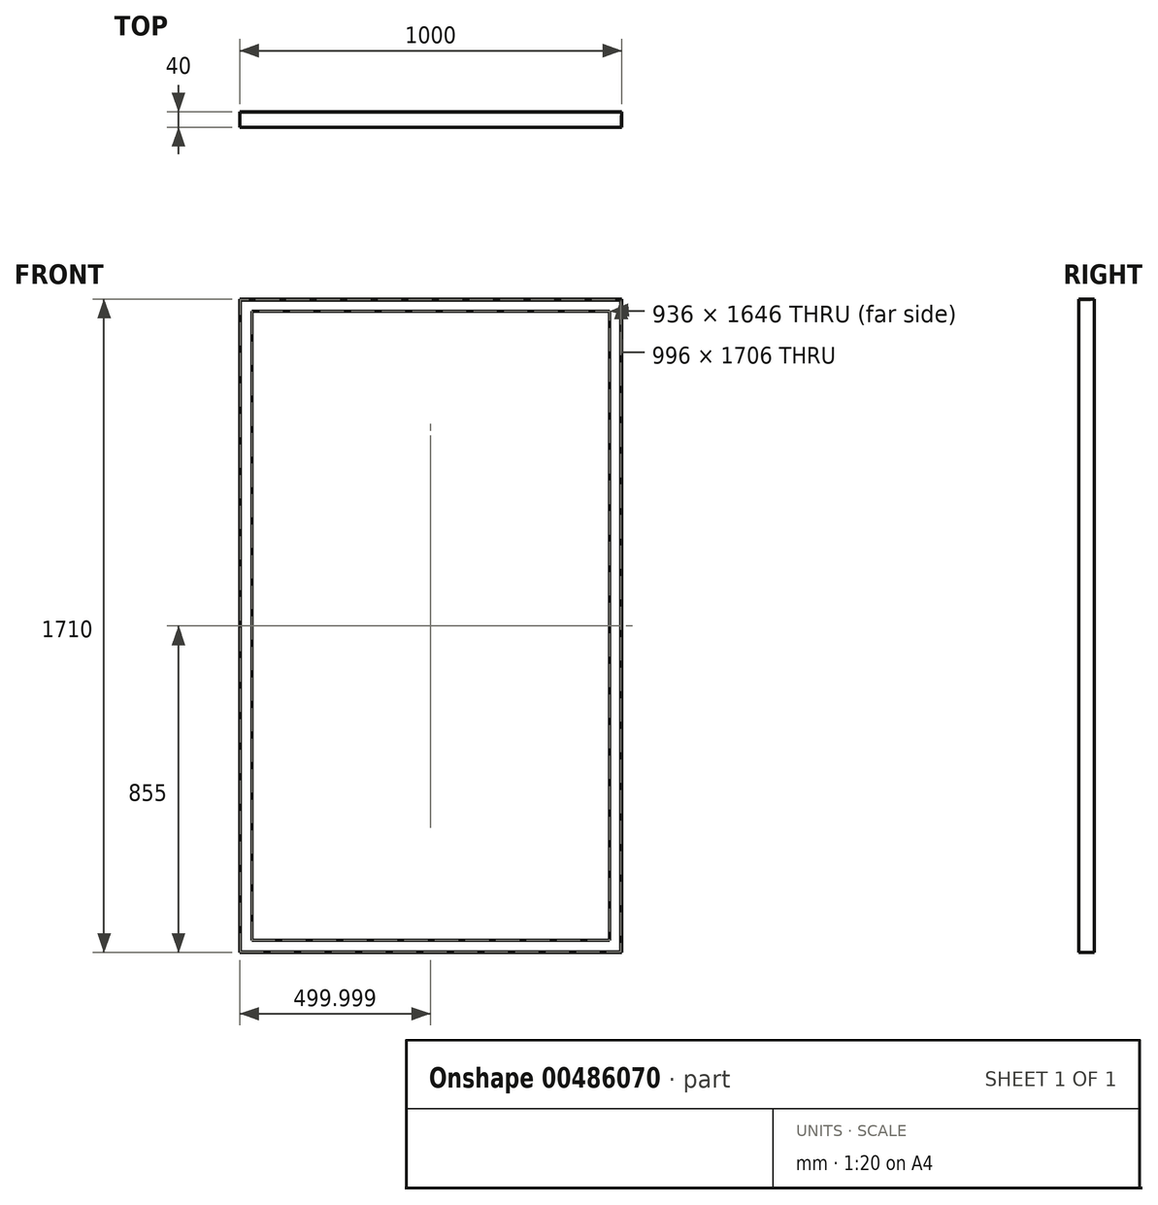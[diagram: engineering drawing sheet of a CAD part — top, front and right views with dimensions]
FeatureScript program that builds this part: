
annotation { "Feature Type Name" : "Feature", "Feature Type Description" : "" }
export const myFeature = defineFeature(function(context is Context, id is Id, definition is map)
    precondition{}
    {
        {
            var Q0;
            Q0=qCreatedBy(makeId("Front.planeOp"),FACE);
            var sketch = newSketch(context, id + "F0", { "sketchPlane" : qUnion([Q0])});
            skLineSegment(sketch, "E0.0", {"start": v(959.78, -40) * mm, "end": v(959.78, -1750) * mm});
            skLineSegment(sketch, "E1.0", {"start": v(-40.22, -40) * mm, "end": v(-40.22, -1750) * mm});
            skLineSegment(sketch, "E2.0", {"start": v(-40.22, -1750) * mm, "end": v(959.78, -1750) * mm});
            skLineSegment(sketch, "E3.0", {"start": v(-38.22, -42) * mm, "end": v(957.78, -42) * mm});
            skLineSegment(sketch, "E4.0", {"start": v(-38.22, -42) * mm, "end": v(-38.22, -1748) * mm});
            skLineSegment(sketch, "E5.0", {"start": v(-38.22, -1748) * mm, "end": v(957.78, -1748) * mm});
            skLineSegment(sketch, "E6.0", {"start": v(957.78, -42) * mm, "end": v(957.78, -1748) * mm});
            skLineSegment(sketch, "E7", {"start": v(959.78, -40) * mm, "end": v(-40.22, -40) * mm});
            skLineSegment(sketch, "E8.0", {"start": v(-38.22, -72) * mm, "end": v(957.78, -72) * mm});
            skLineSegment(sketch, "E9.0", {"start": v(-8.22, -42) * mm, "end": v(-8.22, -1749.66) * mm});
            skLineSegment(sketch, "E10.0", {"start": v(-38.22, -1718) * mm, "end": v(957.78, -1718) * mm});
            skLineSegment(sketch, "E11.0", {"start": v(927.78, -42) * mm, "end": v(927.78, -1749.66) * mm});
            skSolve(sketch);
        }
        {
            var Q0;
            Q0=qSketchRegion(id+"F0",true);
            extrude(context, id + "F1", {"entities" : qUnion([Q0]), "depth" : 40 * mm, "offsetDistance" : 25 * mm});
        }
        {
            var Q0;
            {var subQ0=sQuery(id+"F0.wireOp",EDGE,"E6.0");var subQ1=sQuery(id+"F0.wireOp",EDGE,"E3.0");var subQ2=makeQuery(id+"F0.imprint","INTERSECT",VERTEX,{"derivedFrom":[subQ1,subQ0]});Q0=makeQuery(id+"F0.imprint","IMPRINT",FACE,{"disambiguationData":[TD([[makeQuery(id+"F0.imprint","IMPRINT",EDGE,{"disambiguationData":[TD([[subQ2,1.0]])],"derivedFrom":subQ1}),-1.0]])]});}
            var Q1;
            {var subQ0=sQuery(id+"F0.wireOp",EDGE,"E9.0");var subQ1=sQuery(id+"F0.wireOp",EDGE,"E3.0");var subQ2=makeQuery(id+"F0.imprint","INTERSECT",VERTEX,{"derivedFrom":[subQ1,subQ0]});Q1=makeQuery(id+"F0.imprint","IMPRINT",FACE,{"disambiguationData":[TD([[makeQuery(id+"F0.imprint","IMPRINT",EDGE,{"disambiguationData":[TD([[subQ2,-1.0]])],"derivedFrom":subQ1}),-1.0]])]});}
            var Q2;
            {var subQ0=sQuery(id+"F0.wireOp",EDGE,"E8.0");var subQ1=sQuery(id+"F0.wireOp",EDGE,"E6.0");var subQ2=makeQuery(id+"F0.imprint","INTERSECT",VERTEX,{"derivedFrom":[subQ1,subQ0]});Q2=makeQuery(id+"F0.imprint","IMPRINT",FACE,{"disambiguationData":[TD([[makeQuery(id+"F0.imprint","IMPRINT",EDGE,{"disambiguationData":[TD([[subQ2,-1.0]])],"derivedFrom":subQ1}),-1.0]])]});}
            var Q3;
            {var subQ0=sQuery(id+"F0.wireOp",EDGE,"E4.0");var subQ1=sQuery(id+"F0.wireOp",EDGE,"E3.0");var subQ2=makeQuery(id+"F0.imprint","INTERSECT",VERTEX,{"derivedFrom":[subQ1,subQ0]});Q3=makeQuery(id+"F0.imprint","IMPRINT",FACE,{"disambiguationData":[TD([[makeQuery(id+"F0.imprint","IMPRINT",EDGE,{"disambiguationData":[TD([[subQ2,-1.0]])],"derivedFrom":subQ1}),-1.0]])]});}
            var Q4;
            {var subQ0=sQuery(id+"F0.wireOp",EDGE,"E8.0");var subQ1=sQuery(id+"F0.wireOp",EDGE,"E4.0");var subQ2=makeQuery(id+"F0.imprint","INTERSECT",VERTEX,{"derivedFrom":[subQ1,subQ0]});Q4=makeQuery(id+"F0.imprint","IMPRINT",FACE,{"disambiguationData":[TD([[makeQuery(id+"F0.imprint","IMPRINT",EDGE,{"disambiguationData":[TD([[subQ2,-1.0]])],"derivedFrom":subQ1}),1.0]])]});}
            var Q5;
            {var subQ0=sQuery(id+"F0.wireOp",EDGE,"E5.0");var subQ1=sQuery(id+"F0.wireOp",EDGE,"E4.0");var subQ2=makeQuery(id+"F0.imprint","INTERSECT",VERTEX,{"derivedFrom":[subQ1,subQ0]});Q5=makeQuery(id+"F0.imprint","IMPRINT",FACE,{"disambiguationData":[TD([[makeQuery(id+"F0.imprint","IMPRINT",EDGE,{"disambiguationData":[TD([[subQ2,1.0]])],"derivedFrom":subQ1}),1.0]])]});}
            var Q6;
            {var subQ0=sQuery(id+"F0.wireOp",EDGE,"E9.0");var subQ1=sQuery(id+"F0.wireOp",EDGE,"E5.0");var subQ2=makeQuery(id+"F0.imprint","INTERSECT",VERTEX,{"derivedFrom":[subQ1,subQ0]});Q6=makeQuery(id+"F0.imprint","IMPRINT",FACE,{"disambiguationData":[TD([[makeQuery(id+"F0.imprint","IMPRINT",EDGE,{"disambiguationData":[TD([[subQ2,-1.0]])],"derivedFrom":subQ1}),1.0]])]});}
            var Q7;
            {var subQ0=sQuery(id+"F0.wireOp",EDGE,"E6.0");var subQ1=sQuery(id+"F0.wireOp",EDGE,"E5.0");var subQ2=makeQuery(id+"F0.imprint","INTERSECT",VERTEX,{"derivedFrom":[subQ1,subQ0]});Q7=makeQuery(id+"F0.imprint","IMPRINT",FACE,{"disambiguationData":[TD([[makeQuery(id+"F0.imprint","IMPRINT",EDGE,{"disambiguationData":[TD([[subQ2,1.0]])],"derivedFrom":subQ1}),1.0]])]});}
            extrude(context, id + "F2", {"entities" : qUnion([Q0, Q1, Q2, Q3, Q4, Q5, Q6, Q7]), "depth" : 2 * mm, "offsetDistance" : 25 * mm});
        }
    });
